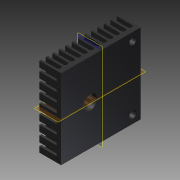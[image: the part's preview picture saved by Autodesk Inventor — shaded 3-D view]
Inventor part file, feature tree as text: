
AUTODESK INVENTOR PART (.ipt)
format: ipt  version: 2015 (Build 190159000, 159)  size: 561,664 bytes
history: native  units: mm
features: extrude x4, pattern_linear x2, hole x1
ambient origin geometry x8: Origin, YZ Plane, XZ Plane, XY Plane, X Axis, Y Axis, Z Axis, Center Point
bodies: Solid1 (feature_tree)
feature tree (7):
  extrude  "Extrusión1"  Depth=40.0mm
  extrude  "Extrusión2"  Depth=11.0mm
  pattern_linear  "Patrón rectangular1"  Spacing1=1.1mm  [1 undecoded]
  extrude  "Extrusión3"  Depth=2.3mm
  pattern_linear  "Patrón rectangular3"  Spacing1=2.141mm  [1 undecoded]
  hole  "Agujero1"  [1 undecoded]
  extrude  "Extrusión5"  Depth=40.0mm TaperAngle=0.0deg
note: 3 required parameter values undecoded (feature->parameter linkage not recoverable at this tier; creation-order binding heuristic only, values carry confidence <= 0.55)
